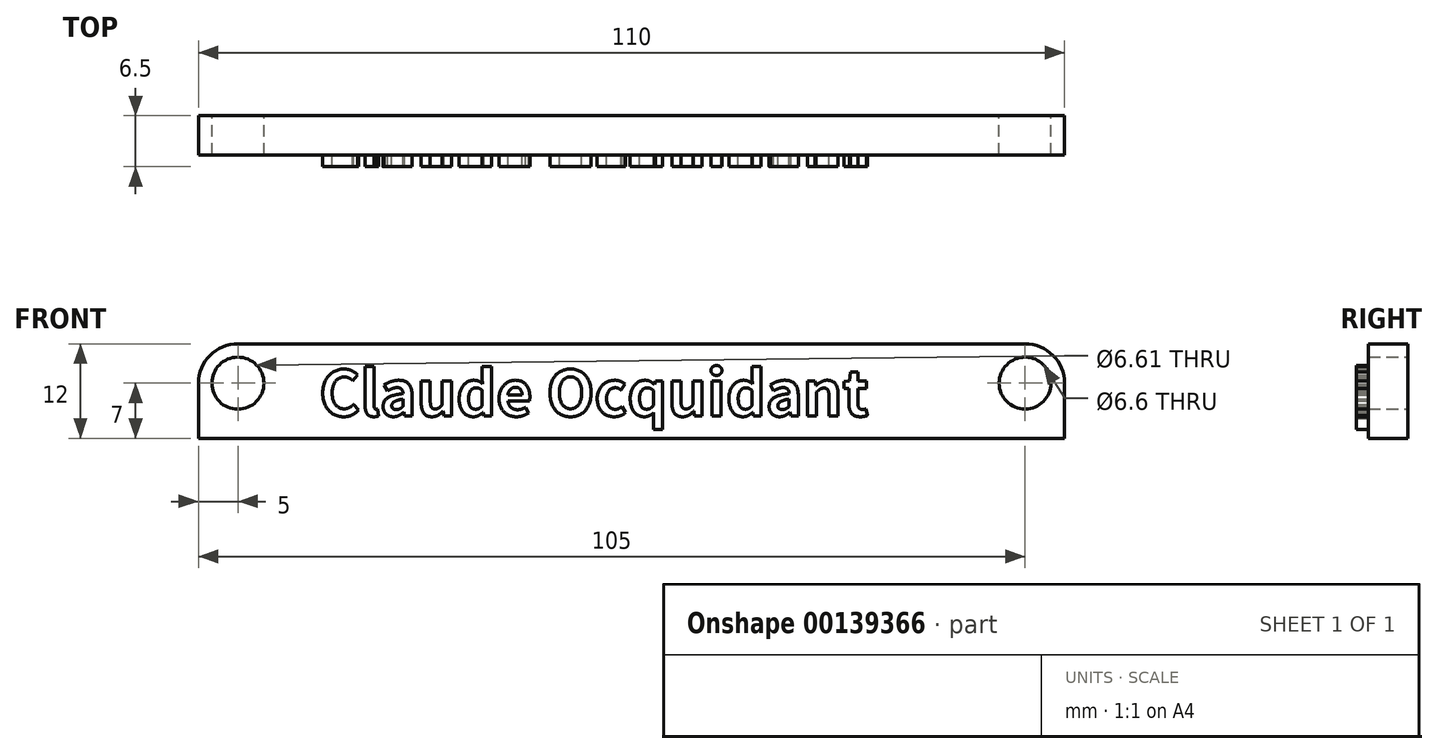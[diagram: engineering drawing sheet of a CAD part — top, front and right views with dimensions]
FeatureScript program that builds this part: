
annotation { "Feature Type Name" : "Feature", "Feature Type Description" : "" }
export const myFeature = defineFeature(function(context is Context, id is Id, definition is map)
    precondition{}
    {
        {
            var Q0;
            Q0=qCreatedBy(makeId("Front.planeOp"),FACE);
            var sketch = newSketch(context, id + "F0", { "sketchPlane" : qUnion([Q0])});
            skLineSegment(sketch, "E0.bottom", {"start": v(-20.2, 12) * mm, "end": v(79.8, 12) * mm});
            skLineSegment(sketch, "E0.top", {"start": v(-25.2, 0) * mm, "end": v(84.8, 0) * mm});
            skLineSegment(sketch, "E0.left", {"start": v(-25.2, 7) * mm, "end": v(-25.2, 0) * mm});
            skLineSegment(sketch, "E0.right", {"start": v(84.8, 7) * mm, "end": v(84.8, 0) * mm});
            skPoint(sketch, "E1.visualSharp", {"position": v(-25.2, 12) * mm});
            skArc(sketch, "E1.filletArc", {"start": v(-20.2, 12) * mm, "mid": v(-23.74, 10.54) * mm, "end": v(-25.2, 7) * mm});
            skPoint(sketch, "E2.visualSharp", {"position": v(84.8, 12) * mm});
            skArc(sketch, "E2.filletArc", {"start": v(84.8, 7) * mm, "mid": v(83.34, 10.54) * mm, "end": v(79.8, 12) * mm});
            skCircle(sketch, "E3", {"center": v(-20.2, 7) * mm, "radius": 3.3 * mm});
            skCircle(sketch, "E4", {"center": v(79.8, 7) * mm, "radius": 3.3 * mm});
            skSolve(sketch);
        }
        {
            var Q0;
            Q0 = qSketchRegion(id + "F0", true);
            extrude(context, id + "F1", {"entities" : qUnion([Q0]), "depth" : 5 * mm});
        }
        {
            var Q0;
            Q0=qCreatedBy(makeId("Front.planeOp"),FACE);
            cPlane(context, id + "F2", {"entities" : qUnion([Q0]), "cplaneType" : CPlaneType.OFFSET, "offset" : 4 * mm, "width" : 150 * mm, "height" : 150 * mm});
        }
        {
            var Q0;
            Q0=qCreatedBy(id+"F2.planeOp",FACE);
            var sketch = newSketch(context, id + "F3", { "sketchPlane" : qUnion([Q0])});
            skText(sketch, "E5", { "text": "Claude Ocquidant \n", "fontName": "NotoSansCJKsc-Bold.otf"});
            const initialGuessF3  = {"E5": [-0.00985, 0.00284, 1, 0, 0.00569]};
            skSetInitialGuess(sketch, initialGuessF3);
            skSolve(sketch);
        }
        {
            var Q0;
            Q0 = qSketchRegion(id + "F3", true);
            extrude(context, id + "F4", {"entities" : qUnion([Q0]), "operationType" : NewBodyOperationType.ADD, "depth" : 2.5 * mm});
        }
    });
